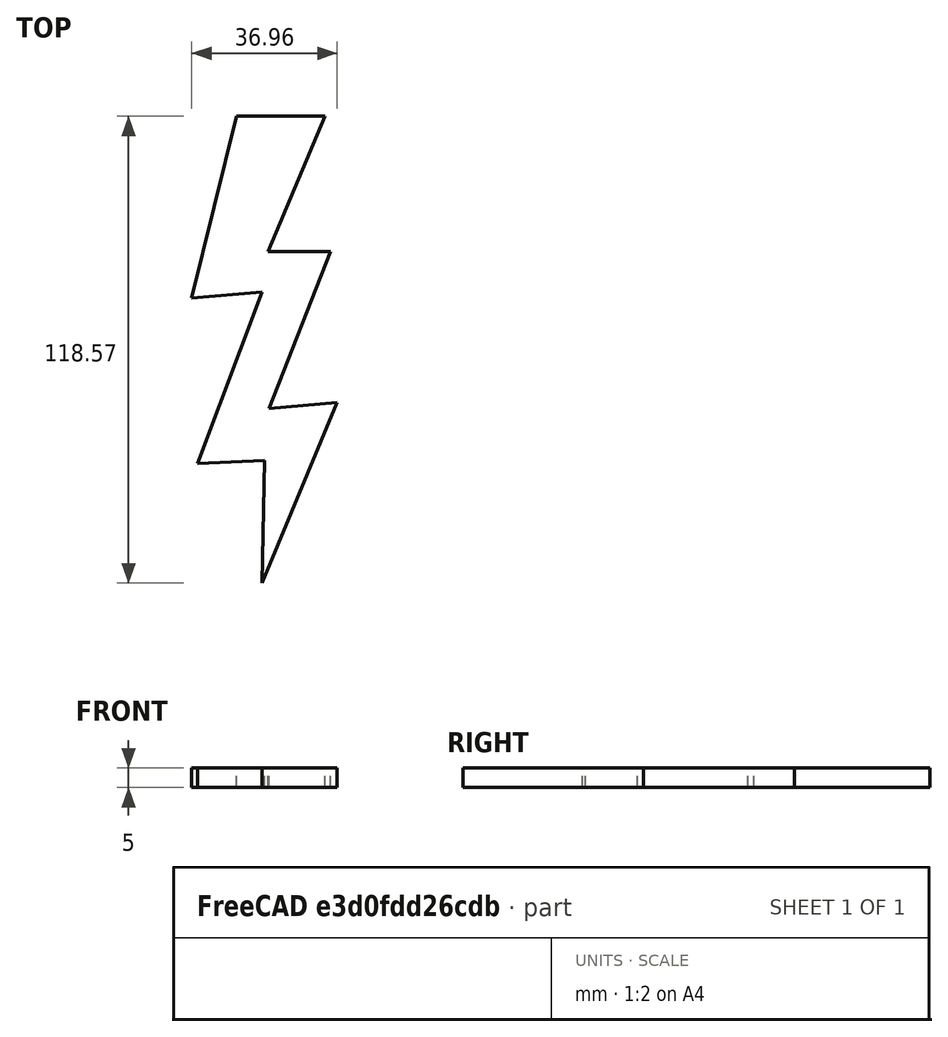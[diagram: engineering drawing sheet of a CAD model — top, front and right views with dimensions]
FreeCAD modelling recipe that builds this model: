
FCSTD DOCUMENT  (FreeCAD 0.21R33694 (Git))
Label: OJT1_T16R03_llamp
License: All rights reserved
LicenseURL: http://en.wikipedia.org/wiki/All_rights_reserved
objects: Sketcher::SketchObject×1, PartDesign::Pad×1, PartDesign::Body×1
note: 4 computed .brp shape members not serialized (recipe doc carries the construction recipe); baked Part::Feature solids carry a one-line shape summary decoded from their .brp

FEATURE [Sketcher::SketchObject] Sketch
  FullyConstrained = false
  MapMode = 5
  Support = -> [XY_Plane]
  sketch-geometry (11):
    g0: LineSegment StartX=-6.51083 StartY=87.4892 StartZ=0 EndX=16.0168 EndY=87.4892 EndZ=0
    g1: LineSegment StartX=16.0168 StartY=87.4892 StartZ=0 EndX=1.45821 EndY=53.1586 EndZ=0
    g2: LineSegment StartX=1.45821 StartY=53.1586 StartZ=0 EndX=17.4313 EndY=53.1586 EndZ=0
    g3: LineSegment StartX=17.4313 StartY=53.1586 StartZ=0 EndX=1.80463 EndY=13.2661 EndZ=0
    g4: LineSegment StartX=1.80463 StartY=13.2661 StartZ=0 EndX=19.0515 EndY=14.806 EndZ=0
    g5: LineSegment StartX=19.0515 StartY=14.806 StartZ=0 EndX=0 EndY=-31.0831 EndZ=0
    g6: LineSegment StartX=0 StartY=-31.0831 StartZ=0 EndX=0.606067 EndY=0 EndZ=0
    g7: LineSegment StartX=0.606067 StartY=0 StartZ=0 EndX=-16.3636 EndY=-0.707069 EndZ=0
    g8: LineSegment StartX=-16.3636 StartY=-0.707069 StartZ=0 EndX=0 EndY=42.8321 EndZ=0
    g9: LineSegment StartX=0 StartY=42.8321 StartZ=0 EndX=-17.9061 EndY=41.2922 EndZ=0
    g10: LineSegment StartX=-17.9061 StartY=41.2922 StartZ=0 EndX=-6.51083 EndY=87.4892 EndZ=0
  constraints (16):
    c: Horizontal(g0)
    c: Coincident(g0,g1)
    c: Coincident(g1,g2)
    c: Horizontal(g2)
    c: Coincident(g2,g3)
    c: Coincident(g3,g4)
    c: Coincident(g4,g5)
    c: PointOnObject(g5,g-2)
    c: Coincident(g5,g6)
    c: PointOnObject(g6,g-1)
    c: Coincident(g6,g7)
    c: Coincident(g7,g8)
    c: PointOnObject(g8,g-2)
    c: Coincident(g8,g9)
    c: Coincident(g9,g10)
    c: Coincident(g10,g0)
FEATURE [PartDesign::Pad] Pad
  Direction = (0,0,1)
  Length = 5
  Length2 = 10
  Profile = -> Sketch
  ReferenceAxis = -> Sketch [N_Axis]
  Type = 0
FEATURE [PartDesign::Body] Body
  Group = -> [Sketch,Pad]
  Origin = -> Origin
  Tip = -> Pad
